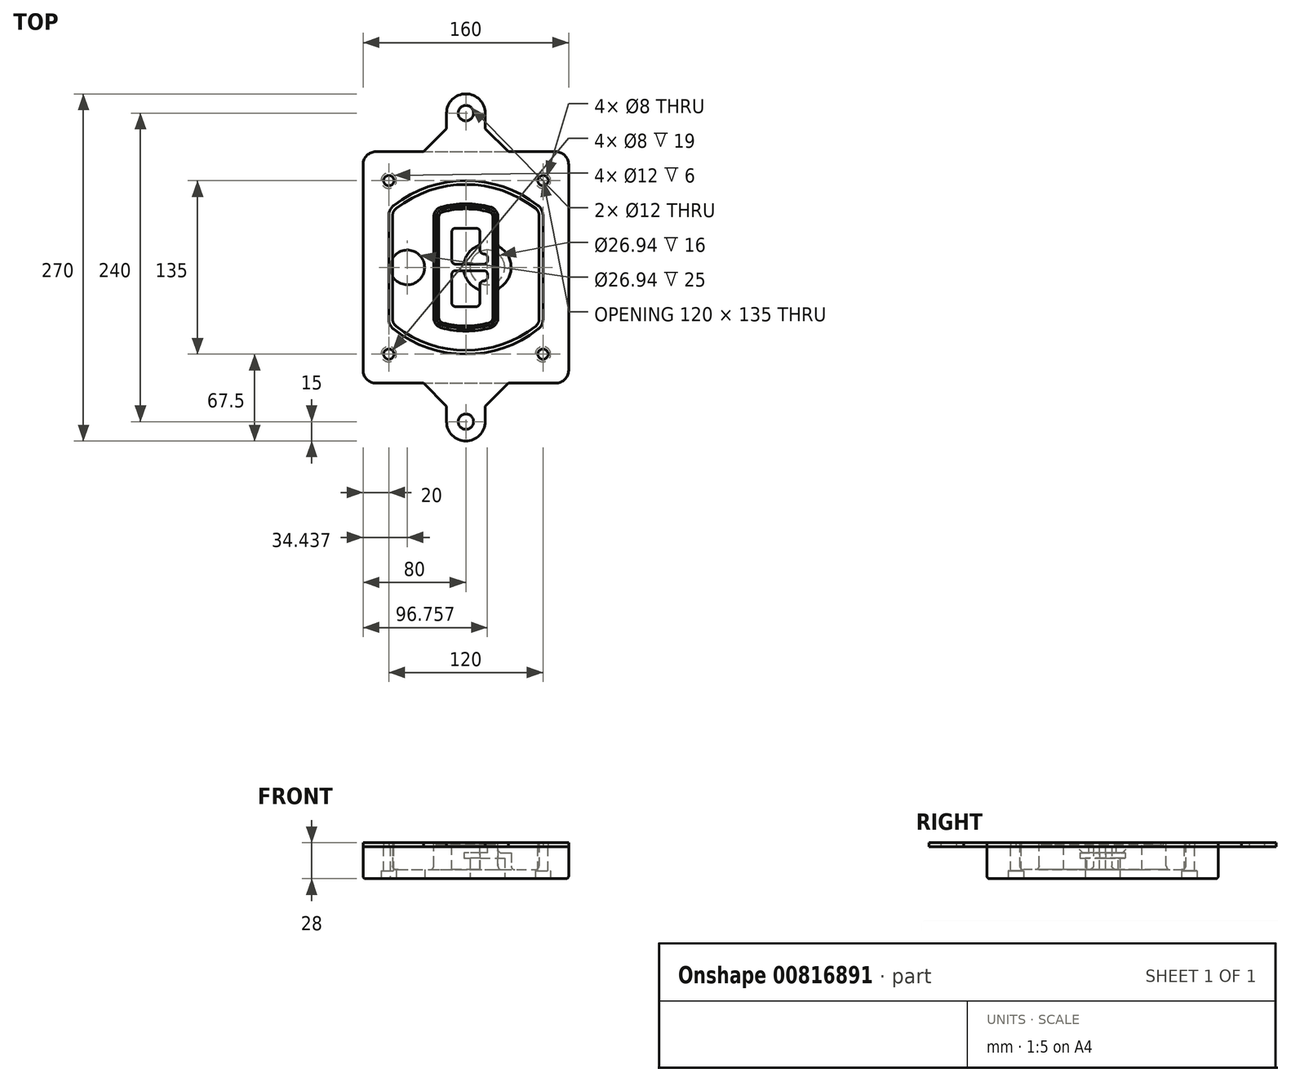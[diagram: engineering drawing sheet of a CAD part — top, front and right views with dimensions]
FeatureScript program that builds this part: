
annotation { "Feature Type Name" : "Feature", "Feature Type Description" : "" }
export const myFeature = defineFeature(function(context is Context, id is Id, definition is map)
    precondition{}
    {
        {
            var Q0;
            Q0=qCreatedBy(makeId("Top.planeOp"),FACE);
            var sketch = newSketch(context, id + "F0", { "sketchPlane" : qUnion([Q0])});
            skPoint(sketch, "E0.rect.middle", {"position": v(0, 0) * mm});
            skLineSegment(sketch, "E1.bottom", {"start": v(-70, -90) * mm, "end": v(70, -90) * mm});
            skLineSegment(sketch, "E1.top", {"start": v(-70, 90) * mm, "end": v(70, 90) * mm});
            skLineSegment(sketch, "E1.left", {"start": v(-80, -80) * mm, "end": v(-80, 80) * mm});
            skLineSegment(sketch, "E1.right", {"start": v(80, -80) * mm, "end": v(80, 80) * mm});
            skLineSegment(sketch, "E2", {"start": v(-80, 90) * mm, "end": v(80, -90) * mm, "construction": true});
            skLineSegment(sketch, "E3", {"start": v(80, 90) * mm, "end": v(-80, -90) * mm, "construction": true});
            skCircle(sketch, "E4", {"center": v(-60, 67.5) * mm, "radius": 4 * mm});
            skCircle(sketch, "E5", {"center": v(60, 67.5) * mm, "radius": 4 * mm});
            skCircle(sketch, "E6", {"center": v(60, -67.5) * mm, "radius": 4 * mm});
            skCircle(sketch, "E7", {"center": v(-60, -67.5) * mm, "radius": 4 * mm});
            skLineSegment(sketch, "E8", {"start": v(-60, 67.5) * mm, "end": v(60, 67.5) * mm, "construction": true});
            skLineSegment(sketch, "E9", {"start": v(60, 67.5) * mm, "end": v(60, -67.5) * mm, "construction": true});
            skLineSegment(sketch, "E10", {"start": v(60, -67.5) * mm, "end": v(-60, -67.5) * mm, "construction": true});
            skLineSegment(sketch, "E11", {"start": v(-60, -67.5) * mm, "end": v(-60, 67.5) * mm, "construction": true});
            skLineSegment(sketch, "E12", {"start": v(-60, 40.3) * mm, "end": v(-60, -40.3) * mm});
            skLineSegment(sketch, "E13", {"start": v(60, 40.3) * mm, "end": v(60, -40.3) * mm});
            skArc(sketch, "E14", {"start": v(56.15, 48.18) * mm, "mid": v(0, 67.5) * mm, "end": v(-56.15, 48.18) * mm});
            skArc(sketch, "E15", {"start": v(-56.15, -48.18) * mm, "mid": v(0, -67.5) * mm, "end": v(56.15, -48.18) * mm});
            skLineSegment(sketch, "E16", {"start": v(-60, 0) * mm, "end": v(60, 0) * mm, "construction": true});
            skPoint(sketch, "E17.visualSharp", {"position": v(-60, -45) * mm});
            skArc(sketch, "E17.filletArc", {"start": v(-60, -40.3) * mm, "mid": v(-58.99, -44.68) * mm, "end": v(-56.15, -48.18) * mm});
            skPoint(sketch, "E18.visualSharp", {"position": v(-60, 45) * mm});
            skArc(sketch, "E18.filletArc", {"start": v(-56.15, 48.18) * mm, "mid": v(-58.99, 44.68) * mm, "end": v(-60, 40.3) * mm});
            skPoint(sketch, "E19.visualSharp", {"position": v(60, 45) * mm});
            skArc(sketch, "E19.filletArc", {"start": v(60, 40.3) * mm, "mid": v(58.99, 44.68) * mm, "end": v(56.15, 48.18) * mm});
            skPoint(sketch, "E20.visualSharp", {"position": v(60, -45) * mm});
            skArc(sketch, "E20.filletArc", {"start": v(56.15, -48.18) * mm, "mid": v(58.99, -44.68) * mm, "end": v(60, -40.3) * mm});
            skPoint(sketch, "E21.visualSharp", {"position": v(-80, 90) * mm});
            skArc(sketch, "E21.filletArc", {"start": v(-70, 90) * mm, "mid": v(-77.07, 87.07) * mm, "end": v(-80, 80) * mm});
            skPoint(sketch, "E22.visualSharp", {"position": v(80, 90) * mm});
            skArc(sketch, "E22.filletArc", {"start": v(80, 80) * mm, "mid": v(77.07, 87.07) * mm, "end": v(70, 90) * mm});
            skPoint(sketch, "E23.visualSharp", {"position": v(80, -90) * mm});
            skArc(sketch, "E23.filletArc", {"start": v(70, -90) * mm, "mid": v(77.07, -87.07) * mm, "end": v(80, -80) * mm});
            skPoint(sketch, "E24.visualSharp", {"position": v(-80, -90) * mm});
            skArc(sketch, "E24.filletArc", {"start": v(-80, -80) * mm, "mid": v(-77.07, -87.07) * mm, "end": v(-70, -90) * mm});
            skArc(sketch, "E25.0", {"start": v(57, 40.3) * mm, "mid": v(56.3, 43.36) * mm, "end": v(54.3, 45.81) * mm});
            skLineSegment(sketch, "E25.1", {"start": v(57, 40.3) * mm, "end": v(57, -40.3) * mm});
            skArc(sketch, "E25.2", {"start": v(54.3, -45.81) * mm, "mid": v(56.3, -43.36) * mm, "end": v(57, -40.3) * mm});
            skArc(sketch, "E25.3", {"start": v(-54.3, -45.81) * mm, "mid": v(0, -64.5) * mm, "end": v(54.3, -45.81) * mm});
            skArc(sketch, "E25.4", {"start": v(-57, -40.3) * mm, "mid": v(-56.3, -43.36) * mm, "end": v(-54.3, -45.81) * mm});
            skArc(sketch, "E25.5", {"start": v(54.3, 45.81) * mm, "mid": v(0, 64.5) * mm, "end": v(-54.3, 45.81) * mm});
            skLineSegment(sketch, "E25.6", {"start": v(-57, 40.3) * mm, "end": v(-57, -40.3) * mm});
            skArc(sketch, "E25.7", {"start": v(-54.3, 45.81) * mm, "mid": v(-56.3, 43.36) * mm, "end": v(-57, 40.3) * mm});
            skArc(sketch, "E26.0", {"start": v(-58.62, 51.33) * mm, "mid": v(-62.58, 46.43) * mm, "end": v(-64, 40.3) * mm});
            skArc(sketch, "E26.1", {"start": v(58.62, 51.33) * mm, "mid": v(0, 71.5) * mm, "end": v(-58.62, 51.33) * mm});
            skArc(sketch, "E26.2", {"start": v(64, 40.3) * mm, "mid": v(62.58, 46.43) * mm, "end": v(58.62, 51.33) * mm});
            skLineSegment(sketch, "E26.3", {"start": v(64, 40.3) * mm, "end": v(64, -40.3) * mm});
            skArc(sketch, "E26.4", {"start": v(58.62, -51.33) * mm, "mid": v(62.58, -46.43) * mm, "end": v(64, -40.3) * mm});
            skLineSegment(sketch, "E26.5", {"start": v(-64, 40.3) * mm, "end": v(-64, -40.3) * mm});
            skArc(sketch, "E26.6", {"start": v(-58.62, -51.33) * mm, "mid": v(0, -71.5) * mm, "end": v(58.62, -51.33) * mm});
            skArc(sketch, "E26.7", {"start": v(-64, -40.3) * mm, "mid": v(-62.58, -46.43) * mm, "end": v(-58.62, -51.33) * mm});
            skSolve(sketch);
        }
        {
            var Q0;
            Q0=makeQuery(id+"F0.imprint","IMPRINT",FACE,{"disambiguationData":[TD([[makeQuery(id+"F0.imprint","IMPRINT",EDGE,{"derivedFrom":sQuery(id+"F0.wireOp",EDGE,"E1.bottom")}),1.0]])]});
            var Q1;
            Q1=makeQuery(id+"F0.imprint","IMPRINT",FACE,{"disambiguationData":[TD([[makeQuery(id+"F0.imprint","IMPRINT",EDGE,{"derivedFrom":sQuery(id+"F0.wireOp",EDGE,"E12")}),1.0]])]});
            var Q2;
            Q2=makeQuery(id+"F0.imprint","IMPRINT",FACE,{"disambiguationData":[TD([[makeQuery(id+"F0.imprint","IMPRINT",EDGE,{"derivedFrom":sQuery(id+"F0.wireOp",EDGE,"E25.0")}),1.0]])]});
            var Q3;
            Q3=makeQuery(id+"F0.imprint","IMPRINT",FACE,{"disambiguationData":[TD([[makeQuery(id+"F0.imprint","IMPRINT",EDGE,{"derivedFrom":sQuery(id+"F0.wireOp",EDGE,"E12")}),-1.0]])]});
            extrude(context, id + "F1", {"entities" : qUnion([Q0, Q1, Q2, Q3]), "oppositeDirection" : true, "depth" : 25 * mm});
        }
        {
            var Q0;
            Q0=makeQuery(id+"F0.imprint","IMPRINT",FACE,{"disambiguationData":[TD([[makeQuery(id+"F0.imprint","IMPRINT",EDGE,{"derivedFrom":sQuery(id+"F0.wireOp",EDGE,"E12")}),1.0]])]});
            extrude(context, id + "F2", {"entities" : qUnion([Q0]), "operationType" : NewBodyOperationType.ADD, "depth" : 3 * mm});
        }
        {
            var Q0;
            Q0=makeQuery(id+"F0.imprint","IMPRINT",FACE,{"disambiguationData":[TD([[makeQuery(id+"F0.imprint","IMPRINT",EDGE,{"derivedFrom":sQuery(id+"F0.wireOp",EDGE,"E25.0")}),1.0]])]});
            extrude(context, id + "F3", {"entities" : qUnion([Q0]), "operationType" : NewBodyOperationType.REMOVE, "oppositeDirection" : true, "depth" : 18 * mm});
        }
        {
            var Q0;
            Q0=makeQuery(id+"F2.opExtrude","CAP_FACE",FACE,{"disambiguationData":[OSD([sQuery(id+"F0.wireOp",EDGE,"E12"),sQuery(id+"F0.wireOp",EDGE,"E13"),sQuery(id+"F0.wireOp",EDGE,"E14"),sQuery(id+"F0.wireOp",EDGE,"E15"),sQuery(id+"F0.wireOp",EDGE,"E17.filletArc"),sQuery(id+"F0.wireOp",EDGE,"E18.filletArc"),sQuery(id+"F0.wireOp",EDGE,"E19.filletArc"),sQuery(id+"F0.wireOp",EDGE,"E20.filletArc"),sQuery(id+"F0.wireOp",EDGE,"E25.0"),sQuery(id+"F0.wireOp",EDGE,"E25.1"),sQuery(id+"F0.wireOp",EDGE,"E25.2"),sQuery(id+"F0.wireOp",EDGE,"E25.3"),sQuery(id+"F0.wireOp",EDGE,"E25.4"),sQuery(id+"F0.wireOp",EDGE,"E25.5"),sQuery(id+"F0.wireOp",EDGE,"E25.6"),sQuery(id+"F0.wireOp",EDGE,"E25.7")])],"isStart":false});
            var sketch = newSketch(context, id + "F4", { "sketchPlane" : qUnion([Q0])});
            skArc(sketch, "E27.0", {"start": v(-19.08, -46.97) * mm, "mid": v(0, -49.5) * mm, "end": v(19.08, -46.97) * mm});
            skArc(sketch, "E28.0", {"start": v(19.08, 46.97) * mm, "mid": v(0, 49.5) * mm, "end": v(-19.08, 46.97) * mm});
            skLineSegment(sketch, "E29", {"start": v(-25, 39.25) * mm, "end": v(-25, -39.25) * mm});
            skLineSegment(sketch, "E30", {"start": v(25, 39.25) * mm, "end": v(25, -39.25) * mm});
            skLineSegment(sketch, "E31", {"start": v(-25, 45.1) * mm, "end": v(25, 45.1) * mm, "construction": true});
            skLineSegment(sketch, "E32", {"start": v(-25, -45.1) * mm, "end": v(25, -45.1) * mm, "construction": true});
            skPoint(sketch, "E33.visualSharp", {"position": v(-25, 45.1) * mm});
            skArc(sketch, "E33.filletArc", {"start": v(-19.08, 46.97) * mm, "mid": v(-23.35, 44.11) * mm, "end": v(-25, 39.25) * mm});
            skPoint(sketch, "E34.visualSharp", {"position": v(25, 45.1) * mm});
            skArc(sketch, "E34.filletArc", {"start": v(25, 39.25) * mm, "mid": v(23.35, 44.11) * mm, "end": v(19.08, 46.97) * mm});
            skPoint(sketch, "E35.visualSharp", {"position": v(25, -45.1) * mm});
            skArc(sketch, "E35.filletArc", {"start": v(19.08, -46.97) * mm, "mid": v(23.35, -44.11) * mm, "end": v(25, -39.25) * mm});
            skPoint(sketch, "E36.visualSharp", {"position": v(-25, -45.1) * mm});
            skArc(sketch, "E36.filletArc", {"start": v(-25, -39.25) * mm, "mid": v(-23.35, -44.11) * mm, "end": v(-19.08, -46.97) * mm});
            skArc(sketch, "E37.0", {"start": v(54.3, 45.81) * mm, "mid": v(0, 64.5) * mm, "end": v(-54.3, 45.81) * mm});
            skArc(sketch, "E37.1", {"start": v(-54.3, 45.81) * mm, "mid": v(-56.3, 43.36) * mm, "end": v(-57, 40.3) * mm});
            skLineSegment(sketch, "E37.2", {"start": v(-57, 40.3) * mm, "end": v(-57, -40.3) * mm});
            skArc(sketch, "E37.3", {"start": v(-57, -40.3) * mm, "mid": v(-56.3, -43.36) * mm, "end": v(-54.3, -45.81) * mm});
            skArc(sketch, "E37.4", {"start": v(-54.3, -45.81) * mm, "mid": v(0, -64.5) * mm, "end": v(54.3, -45.81) * mm});
            skArc(sketch, "E37.5", {"start": v(54.3, -45.81) * mm, "mid": v(56.3, -43.36) * mm, "end": v(57, -40.3) * mm});
            skLineSegment(sketch, "E37.6", {"start": v(57, 40.3) * mm, "end": v(57, -40.3) * mm});
            skArc(sketch, "E37.7", {"start": v(57, 40.3) * mm, "mid": v(56.3, 43.36) * mm, "end": v(54.3, 45.81) * mm});
            skLineSegment(sketch, "E38.0", {"start": v(23, 39.25) * mm, "end": v(23, -39.25) * mm});
            skArc(sketch, "E38.1", {"start": v(18.56, -45.04) * mm, "mid": v(21.76, -42.9) * mm, "end": v(23, -39.25) * mm});
            skArc(sketch, "E38.2", {"start": v(-18.56, -45.04) * mm, "mid": v(0, -47.5) * mm, "end": v(18.56, -45.04) * mm});
            skArc(sketch, "E38.3", {"start": v(-23, -39.25) * mm, "mid": v(-21.76, -42.9) * mm, "end": v(-18.56, -45.04) * mm});
            skLineSegment(sketch, "E38.4", {"start": v(-23, 39.25) * mm, "end": v(-23, -39.25) * mm});
            skArc(sketch, "E38.5", {"start": v(23, 39.25) * mm, "mid": v(21.76, 42.9) * mm, "end": v(18.56, 45.04) * mm});
            skArc(sketch, "E38.6", {"start": v(-18.56, 45.04) * mm, "mid": v(-21.76, 42.9) * mm, "end": v(-23, 39.25) * mm});
            skArc(sketch, "E38.7", {"start": v(18.56, 45.04) * mm, "mid": v(0, 47.5) * mm, "end": v(-18.56, 45.04) * mm});
            skArc(sketch, "E39.0", {"start": v(21, 39.25) * mm, "mid": v(20.18, 41.68) * mm, "end": v(18.04, 43.1) * mm});
            skLineSegment(sketch, "E39.1", {"start": v(21, 39.25) * mm, "end": v(21, -39.25) * mm});
            skArc(sketch, "E39.2", {"start": v(18.04, -43.1) * mm, "mid": v(20.18, -41.68) * mm, "end": v(21, -39.25) * mm});
            skArc(sketch, "E39.3", {"start": v(-18.04, -43.1) * mm, "mid": v(0, -45.5) * mm, "end": v(18.04, -43.1) * mm});
            skArc(sketch, "E39.4", {"start": v(-21, -39.25) * mm, "mid": v(-20.18, -41.68) * mm, "end": v(-18.04, -43.1) * mm});
            skArc(sketch, "E39.5", {"start": v(18.04, 43.1) * mm, "mid": v(0, 45.5) * mm, "end": v(-18.04, 43.1) * mm});
            skLineSegment(sketch, "E39.6", {"start": v(-21, 39.25) * mm, "end": v(-21, -39.25) * mm});
            skArc(sketch, "E39.7", {"start": v(-18.04, 43.1) * mm, "mid": v(-20.18, 41.68) * mm, "end": v(-21, 39.25) * mm});
            skLineSegment(sketch, "E40", {"start": v(-25, 0) * mm, "end": v(25, 0) * mm, "construction": true});
            skLineSegment(sketch, "E41", {"start": v(-11, 5.5) * mm, "end": v(-11, 27.5) * mm});
            skLineSegment(sketch, "E42", {"start": v(-8, 30.5) * mm, "end": v(8, 30.5) * mm});
            skLineSegment(sketch, "E43", {"start": v(11, 27.5) * mm, "end": v(11, 13.5) * mm});
            skLineSegment(sketch, "E44", {"start": v(14, 10.5) * mm, "end": v(14, 10.5) * mm});
            skLineSegment(sketch, "E45", {"start": v(17, 7.5) * mm, "end": v(17, 5.5) * mm});
            skLineSegment(sketch, "E46", {"start": v(14, 2.5) * mm, "end": v(-8, 2.5) * mm});
            skPoint(sketch, "E47.visualSharp", {"position": v(-11, 30.5) * mm});
            skArc(sketch, "E47.filletArc", {"start": v(-8, 30.5) * mm, "mid": v(-10.12, 29.62) * mm, "end": v(-11, 27.5) * mm});
            skPoint(sketch, "E48.visualSharp", {"position": v(11, 30.5) * mm});
            skArc(sketch, "E48.filletArc", {"start": v(11, 27.5) * mm, "mid": v(10.12, 29.62) * mm, "end": v(8, 30.5) * mm});
            skPoint(sketch, "E49.visualSharp", {"position": v(11, 10.5) * mm});
            skArc(sketch, "E49.filletArc", {"start": v(11, 13.5) * mm, "mid": v(11.88, 11.38) * mm, "end": v(14, 10.5) * mm});
            skPoint(sketch, "E50.visualSharp", {"position": v(17, 10.5) * mm});
            skArc(sketch, "E50.filletArc", {"start": v(17, 7.5) * mm, "mid": v(16.12, 9.62) * mm, "end": v(14, 10.5) * mm});
            skPoint(sketch, "E51.visualSharp", {"position": v(17, 2.5) * mm});
            skArc(sketch, "E51.filletArc", {"start": v(14, 2.5) * mm, "mid": v(16.12, 3.38) * mm, "end": v(17, 5.5) * mm});
            skPoint(sketch, "E52.visualSharp", {"position": v(-11, 2.5) * mm});
            skArc(sketch, "E52.filletArc", {"start": v(-11, 5.5) * mm, "mid": v(-10.12, 3.38) * mm, "end": v(-8, 2.5) * mm});
            skLineSegment(sketch, "E53.0.MirrorCS", {"start": v(14, -2.5) * mm, "end": v(-8, -2.5) * mm});
            skArc(sketch, "E54.0.MirrorCS", {"start": v(-11, -5.5) * mm, "mid": v(-10.12, -3.38) * mm, "end": v(-8, -2.5) * mm});
            skLineSegment(sketch, "E55.0.MirrorCS", {"start": v(-11, -5.5) * mm, "end": v(-11, -27.5) * mm});
            skArc(sketch, "E56.0.MirrorCS", {"start": v(-8, -30.5) * mm, "mid": v(-10.12, -29.62) * mm, "end": v(-11, -27.5) * mm});
            skLineSegment(sketch, "E57.0.MirrorCS", {"start": v(-8, -30.5) * mm, "end": v(8, -30.5) * mm});
            skArc(sketch, "E58.0.MirrorCS", {"start": v(11, -27.5) * mm, "mid": v(10.12, -29.62) * mm, "end": v(8, -30.5) * mm});
            skLineSegment(sketch, "E59.0.MirrorCS", {"start": v(11, -27.5) * mm, "end": v(11, -13.5) * mm});
            skArc(sketch, "E60.0.MirrorCS", {"start": v(11, -13.5) * mm, "mid": v(11.88, -11.38) * mm, "end": v(14, -10.5) * mm});
            skArc(sketch, "E61.0.MirrorCS", {"start": v(17, -7.5) * mm, "mid": v(16.12, -9.62) * mm, "end": v(14, -10.5) * mm});
            skLineSegment(sketch, "E62.0.MirrorCS", {"start": v(17, -7.5) * mm, "end": v(17, -5.5) * mm});
            skArc(sketch, "E63.0.MirrorCS", {"start": v(14, -2.5) * mm, "mid": v(16.12, -3.38) * mm, "end": v(17, -5.5) * mm});
            skSolve(sketch);
        }
        {
            var Q0;
            Q0=makeQuery(id+"F4.imprint","IMPRINT",FACE,{"disambiguationData":[TD([[makeQuery(id+"F4.imprint","IMPRINT",EDGE,{"derivedFrom":sQuery(id+"F4.wireOp",EDGE,"E27.0")}),1.0]])]});
            var Q1;
            Q1=makeQuery(id+"F4.imprint","IMPRINT",FACE,{"disambiguationData":[TD([[makeQuery(id+"F4.imprint","IMPRINT",EDGE,{"derivedFrom":sQuery(id+"F4.wireOp",EDGE,"E38.0")}),-1.0]])]});
            var Q2;
            Q2=makeQuery(id+"F4.imprint","IMPRINT",FACE,{"disambiguationData":[TD([[makeQuery(id+"F4.imprint","IMPRINT",EDGE,{"derivedFrom":sQuery(id+"F4.wireOp",EDGE,"E39.0")}),1.0]])]});
            extrude(context, id + "F5", {"entities" : qUnion([Q0, Q1, Q2]), "operationType" : NewBodyOperationType.ADD, "endBound" : BoundingType.UP_TO_NEXT, "oppositeDirection" : true, "depth" : 25 * mm});
        }
        {
            var Q0;
            Q0=makeQuery(id+"F4.imprint","IMPRINT",FACE,{"disambiguationData":[TD([[makeQuery(id+"F4.imprint","IMPRINT",EDGE,{"derivedFrom":sQuery(id+"F4.wireOp",EDGE,"E38.0")}),-1.0]])]});
            extrude(context, id + "F6", {"entities" : qUnion([Q0]), "operationType" : NewBodyOperationType.REMOVE, "oppositeDirection" : true, "depth" : 2 * mm});
        }
        {
            var Q0;
            Q0=makeQuery(id+"F1.opExtrude","CAP_FACE",FACE,{"disambiguationData":[OSD([sQuery(id+"F0.wireOp",EDGE,"E1.bottom"),sQuery(id+"F0.wireOp",EDGE,"E1.top"),sQuery(id+"F0.wireOp",EDGE,"E1.left"),sQuery(id+"F0.wireOp",EDGE,"E1.right"),sQuery(id+"F0.wireOp",EDGE,"E4"),sQuery(id+"F0.wireOp",EDGE,"E5"),sQuery(id+"F0.wireOp",EDGE,"E6"),sQuery(id+"F0.wireOp",EDGE,"E7"),sQuery(id+"F0.wireOp",EDGE,"E21.filletArc"),sQuery(id+"F0.wireOp",EDGE,"E22.filletArc"),sQuery(id+"F0.wireOp",EDGE,"E23.filletArc"),sQuery(id+"F0.wireOp",EDGE,"E24.filletArc")])],"isStart":false});
            var sketch = newSketch(context, id + "F7", { "sketchPlane" : qUnion([Q0])});
            skCircle(sketch, "E64", {"center": v(16.76, 0) * mm, "radius": 13.47 * mm});
            skCircle(sketch, "E65", {"center": v(-45.56, 0) * mm, "radius": 13.47 * mm});
            skLineSegment(sketch, "E66", {"start": v(80, 0) * mm, "end": v(-80, 0) * mm});
            skCircle(sketch, "E67", {"center": v(16.76, 0) * mm, "radius": 18.47 * mm});
            skCircle(sketch, "E68", {"center": v(60, -67.5) * mm, "radius": 6 * mm});
            skCircle(sketch, "E69", {"center": v(-60, -67.5) * mm, "radius": 6 * mm});
            skCircle(sketch, "E70", {"center": v(-60, 67.5) * mm, "radius": 6 * mm});
            skCircle(sketch, "E71", {"center": v(60, 67.5) * mm, "radius": 6 * mm});
            skSolve(sketch);
        }
        {
            var Q0;
            {var subQ1=sQuery(id+"F7.wireOp",EDGE,"E66");var subQ4=sQuery(id+"F7.wireOp",EDGE,"E64");var subQ6=makeQuery(id+"F7.imprint","INTERSECT",VERTEX,{"disambiguationData":[OD(0.0)],"derivedFrom":[subQ4,subQ1]});Q0=makeQuery(id+"F7.imprint","IMPRINT",FACE,{"disambiguationData":[TD([[makeQuery(id+"F7.imprint","IMPRINT",EDGE,{"disambiguationData":[TD([[subQ6,-1.0]])],"derivedFrom":subQ4}),-1.0]])]});}
            var Q1;
            {var subQ0=sQuery(id+"F7.wireOp",EDGE,"E66");var subQ1=sQuery(id+"F7.wireOp",EDGE,"E64");var subQ3=makeQuery(id+"F7.imprint","INTERSECT",VERTEX,{"disambiguationData":[OD(0.0)],"derivedFrom":[subQ1,subQ0]});Q1=makeQuery(id+"F7.imprint","IMPRINT",FACE,{"disambiguationData":[TD([[makeQuery(id+"F7.imprint","IMPRINT",EDGE,{"disambiguationData":[TD([[subQ3,-1.0]])],"derivedFrom":subQ1}),1.0]])]});}
            var Q2;
            {var subQ0=sQuery(id+"F7.wireOp",EDGE,"E66");var subQ1=sQuery(id+"F7.wireOp",EDGE,"E64");var subQ3=makeQuery(id+"F7.imprint","INTERSECT",VERTEX,{"disambiguationData":[OD(0.0)],"derivedFrom":[subQ1,subQ0]});Q2=makeQuery(id+"F7.imprint","IMPRINT",FACE,{"disambiguationData":[TD([[makeQuery(id+"F7.imprint","IMPRINT",EDGE,{"disambiguationData":[TD([[subQ3,1.0]])],"derivedFrom":subQ1}),1.0]])]});}
            var Q3;
            {var subQ1=sQuery(id+"F7.wireOp",EDGE,"E66");var subQ4=sQuery(id+"F7.wireOp",EDGE,"E64");var subQ6=makeQuery(id+"F7.imprint","INTERSECT",VERTEX,{"disambiguationData":[OD(0.0)],"derivedFrom":[subQ4,subQ1]});Q3=makeQuery(id+"F7.imprint","IMPRINT",FACE,{"disambiguationData":[TD([[makeQuery(id+"F7.imprint","IMPRINT",EDGE,{"disambiguationData":[TD([[subQ6,1.0]])],"derivedFrom":subQ4}),-1.0]])]});}
            extrude(context, id + "F8", {"entities" : qUnion([Q0, Q1, Q2, Q3]), "operationType" : NewBodyOperationType.ADD, "oppositeDirection" : true, "depth" : 20 * mm});
        }
        {
            var Q0;
            {var subQ0=sQuery(id+"F7.wireOp",EDGE,"E66");var subQ1=sQuery(id+"F7.wireOp",EDGE,"E64");var subQ3=makeQuery(id+"F7.imprint","INTERSECT",VERTEX,{"disambiguationData":[OD(0.0)],"derivedFrom":[subQ1,subQ0]});Q0=makeQuery(id+"F7.imprint","IMPRINT",FACE,{"disambiguationData":[TD([[makeQuery(id+"F7.imprint","IMPRINT",EDGE,{"disambiguationData":[TD([[subQ3,-1.0]])],"derivedFrom":subQ1}),1.0]])]});}
            var Q1;
            {var subQ0=sQuery(id+"F7.wireOp",EDGE,"E66");var subQ1=sQuery(id+"F7.wireOp",EDGE,"E64");var subQ3=makeQuery(id+"F7.imprint","INTERSECT",VERTEX,{"disambiguationData":[OD(0.0)],"derivedFrom":[subQ1,subQ0]});Q1=makeQuery(id+"F7.imprint","IMPRINT",FACE,{"disambiguationData":[TD([[makeQuery(id+"F7.imprint","IMPRINT",EDGE,{"disambiguationData":[TD([[subQ3,1.0]])],"derivedFrom":subQ1}),1.0]])]});}
            extrude(context, id + "F9", {"entities" : qUnion([Q0, Q1]), "operationType" : NewBodyOperationType.REMOVE, "oppositeDirection" : true, "depth" : 16 * mm});
        }
        {
            var Q0;
            {var subQ0=sQuery(id+"F7.wireOp",EDGE,"E66");var subQ1=sQuery(id+"F7.wireOp",EDGE,"E65");var subQ3=makeQuery(id+"F7.imprint","INTERSECT",VERTEX,{"disambiguationData":[OD(0.0)],"derivedFrom":[subQ1,subQ0]});Q0=makeQuery(id+"F7.imprint","IMPRINT",FACE,{"disambiguationData":[TD([[makeQuery(id+"F7.imprint","IMPRINT",EDGE,{"disambiguationData":[TD([[subQ3,-1.0]])],"derivedFrom":subQ1}),1.0]])]});}
            var Q1;
            {var subQ0=sQuery(id+"F7.wireOp",EDGE,"E66");var subQ1=sQuery(id+"F7.wireOp",EDGE,"E65");var subQ3=makeQuery(id+"F7.imprint","INTERSECT",VERTEX,{"disambiguationData":[OD(0.0)],"derivedFrom":[subQ1,subQ0]});Q1=makeQuery(id+"F7.imprint","IMPRINT",FACE,{"disambiguationData":[TD([[makeQuery(id+"F7.imprint","IMPRINT",EDGE,{"disambiguationData":[TD([[subQ3,1.0]])],"derivedFrom":subQ1}),1.0]])]});}
            extrude(context, id + "F10", {"entities" : qUnion([Q0, Q1]), "operationType" : NewBodyOperationType.REMOVE, "oppositeDirection" : true, "depth" : 25 * mm});
        }
        {
            var Q0;
            Q0=makeQuery(id+"F7.imprint","IMPRINT",FACE,{"disambiguationData":[TD([[makeQuery(id+"F7.imprint","IMPRINT",EDGE,{"derivedFrom":sQuery(id+"F7.wireOp",EDGE,"E68")}),1.0]])]});
            var Q1;
            Q1=makeQuery(id+"F7.imprint","IMPRINT",FACE,{"disambiguationData":[TD([[makeQuery(id+"F7.imprint","IMPRINT",EDGE,{"derivedFrom":makeQuery(id+"F1.opExtrude","CAP_EDGE",EDGE,{"disambiguationData":[OSD([sQuery(id+"F0.wireOp",EDGE,"E5")])],"isStart":false})}),-1.0]])]});
            var Q2;
            Q2=makeQuery(id+"F7.imprint","IMPRINT",FACE,{"disambiguationData":[TD([[makeQuery(id+"F7.imprint","IMPRINT",EDGE,{"derivedFrom":sQuery(id+"F7.wireOp",EDGE,"E69")}),1.0]])]});
            var Q3;
            Q3=makeQuery(id+"F7.imprint","IMPRINT",FACE,{"disambiguationData":[TD([[makeQuery(id+"F7.imprint","IMPRINT",EDGE,{"derivedFrom":makeQuery(id+"F1.opExtrude","CAP_EDGE",EDGE,{"disambiguationData":[OSD([sQuery(id+"F0.wireOp",EDGE,"E4")])],"isStart":false})}),-1.0]])]});
            var Q4;
            Q4=makeQuery(id+"F7.imprint","IMPRINT",FACE,{"disambiguationData":[TD([[makeQuery(id+"F7.imprint","IMPRINT",EDGE,{"derivedFrom":sQuery(id+"F7.wireOp",EDGE,"E70")}),1.0]])]});
            var Q5;
            Q5=makeQuery(id+"F7.imprint","IMPRINT",FACE,{"disambiguationData":[TD([[makeQuery(id+"F7.imprint","IMPRINT",EDGE,{"derivedFrom":makeQuery(id+"F1.opExtrude","CAP_EDGE",EDGE,{"disambiguationData":[OSD([sQuery(id+"F0.wireOp",EDGE,"E7")])],"isStart":false})}),-1.0]])]});
            var Q6;
            Q6=makeQuery(id+"F7.imprint","IMPRINT",FACE,{"disambiguationData":[TD([[makeQuery(id+"F7.imprint","IMPRINT",EDGE,{"derivedFrom":sQuery(id+"F7.wireOp",EDGE,"E71")}),1.0]])]});
            var Q7;
            Q7=makeQuery(id+"F7.imprint","IMPRINT",FACE,{"disambiguationData":[TD([[makeQuery(id+"F7.imprint","IMPRINT",EDGE,{"derivedFrom":makeQuery(id+"F1.opExtrude","CAP_EDGE",EDGE,{"disambiguationData":[OSD([sQuery(id+"F0.wireOp",EDGE,"E6")])],"isStart":false})}),-1.0]])]});
            extrude(context, id + "F11", {"entities" : qUnion([Q0, Q1, Q2, Q3, Q4, Q5, Q6, Q7]), "operationType" : NewBodyOperationType.REMOVE, "oppositeDirection" : true, "depth" : 6 * mm});
        }
        {
            var Q0;
            Q0=makeQuery(id+"F9.boolean.opBoolean","COPY",FACE,{"derivedFrom":makeQuery(id+"F9.opExtrude","CAP_FACE",FACE,{"disambiguationData":[OSD([sQuery(id+"F7.wireOp",EDGE,"E64")])],"isStart":false})});
            var sketch = newSketch(context, id + "F12", { "sketchPlane" : qUnion([Q0])});
            skArc(sketch, "E72.0", {"start": v(11, 17.55) * mm, "mid": v(2.57, 11.82) * mm, "end": v(-1.54, 2.5) * mm});
            skArc(sketch, "E72.1", {"start": v(-1.54, -2.5) * mm, "mid": v(2.57, -11.82) * mm, "end": v(11, -17.55) * mm});
            skLineSegment(sketch, "E73", {"start": v(-1.54, -2.5) * mm, "end": v(14, -2.5) * mm});
            skLineSegment(sketch, "E74.0", {"start": v(14, 2.5) * mm, "end": v(-1.54, 2.5) * mm});
            skArc(sketch, "E74.1", {"start": v(14, 2.5) * mm, "mid": v(16.12, 3.38) * mm, "end": v(17, 5.5) * mm});
            skLineSegment(sketch, "E74.2", {"start": v(17, 7.5) * mm, "end": v(17, 5.5) * mm});
            skArc(sketch, "E74.3", {"start": v(17, 7.5) * mm, "mid": v(16.12, 9.62) * mm, "end": v(14, 10.5) * mm});
            skArc(sketch, "E74.4", {"start": v(11, 13.5) * mm, "mid": v(11.88, 11.38) * mm, "end": v(14, 10.5) * mm});
            skLineSegment(sketch, "E74.5", {"start": v(11, 17.55) * mm, "end": v(11, 13.5) * mm});
            skLineSegment(sketch, "E74.7", {"start": v(14, -2.5) * mm, "end": v(-1.54, -2.5) * mm});
            skArc(sketch, "E74.8", {"start": v(14, -2.5) * mm, "mid": v(16.12, -3.38) * mm, "end": v(17, -5.5) * mm});
            skLineSegment(sketch, "E74.9", {"start": v(17, -7.5) * mm, "end": v(17, -5.5) * mm});
            skArc(sketch, "E74.10", {"start": v(17, -7.5) * mm, "mid": v(16.12, -9.62) * mm, "end": v(14, -10.5) * mm});
            skArc(sketch, "E74.11", {"start": v(11, -13.5) * mm, "mid": v(11.88, -11.38) * mm, "end": v(14, -10.5) * mm});
            skLineSegment(sketch, "E74.12", {"start": v(11, -17.55) * mm, "end": v(11, -13.5) * mm});
            skPoint(sketch, "E75.orphan", {"position": v(11, -27.5) * mm});
            skPoint(sketch, "E76.orphan", {"position": v(-8, -2.5) * mm});
            skPoint(sketch, "E77.orphan", {"position": v(-8, 2.5) * mm});
            skPoint(sketch, "E78.orphan", {"position": v(11, 27.5) * mm});
            skSolve(sketch);
        }
        {
            var Q0;
            {var subQ7=sQuery(id+"F12.wireOp",EDGE,"E72.0");var subQ14=sQuery(id+"F12.wireOp",EDGE,"E72.1");var subQ16=sQuery(id+"F12.wireOp",EDGE,"E74.1");var subQ18=sQuery(id+"F12.wireOp",EDGE,"E74.8");Q0=qUnion([makeQuery(id+"F12.imprint","IMPRINT",FACE,{"disambiguationData":[TD([[makeQuery(id+"F12.imprint","IMPRINT",EDGE,{"derivedFrom":subQ7}),1.0]])]}),makeQuery(id+"F12.imprint","IMPRINT",FACE,{"disambiguationData":[TD([[makeQuery(id+"F12.imprint","IMPRINT",EDGE,{"derivedFrom":subQ14}),1.0]])]}),makeQuery(id+"F12.imprint","IMPRINT",FACE,{"disambiguationData":[TD([[makeQuery(id+"F12.imprint","IMPRINT",EDGE,{"derivedFrom":subQ16}),1.0]])]}),makeQuery(id+"F12.imprint","IMPRINT",FACE,{"disambiguationData":[TD([[makeQuery(id+"F12.imprint","IMPRINT",EDGE,{"derivedFrom":subQ18}),-1.0]])]})]);}
            var Q1;
            Q1=makeQuery(id+"F5.boolean.opBoolean","SPLIT",FACE,{"disambiguationData":[TD([makeQuery(id+"F5.opExtrude","SWEPT_FACE",FACE,{"disambiguationData":[OSD([sQuery(id+"F4.wireOp",EDGE,"E41")])]})])],"derivedFrom":makeQuery(id+"F3.boolean.opBoolean","COPY",FACE,{"derivedFrom":makeQuery(id+"F3.opExtrude","CAP_FACE",FACE,{"disambiguationData":[OSD([sQuery(id+"F0.wireOp",EDGE,"E25.0"),sQuery(id+"F0.wireOp",EDGE,"E25.1"),sQuery(id+"F0.wireOp",EDGE,"E25.2"),sQuery(id+"F0.wireOp",EDGE,"E25.3"),sQuery(id+"F0.wireOp",EDGE,"E25.4"),sQuery(id+"F0.wireOp",EDGE,"E25.5"),sQuery(id+"F0.wireOp",EDGE,"E25.6"),sQuery(id+"F0.wireOp",EDGE,"E25.7")])],"isStart":false})})});
            extrude(context, id + "F13", {"entities" : qUnion([Q0]), "operationType" : NewBodyOperationType.REMOVE, "endBound" : BoundingType.UP_TO_SURFACE, "endBoundEntityFace" : qUnion([Q1]), "depth" : 25 * mm});
        }
        {
            var Q0;
            Q0=makeQuery(id+"F3.boolean.opBoolean","COPY",EDGE,{"derivedFrom":makeQuery(id+"F3.opExtrude","CAP_EDGE",EDGE,{"disambiguationData":[OSD([sQuery(id+"F0.wireOp",EDGE,"E25.6")])],"isStart":false})});
            var Q1;
            Q1=makeQuery(id+"F8.boolean.opBoolean","INTERSECT",EDGE,{"derivedFrom":[makeQuery(id+"F5.opExtrude","SWEPT_FACE",FACE,{"disambiguationData":[OSD([sQuery(id+"F4.wireOp",EDGE,"E30")])]}),makeQuery(id+"F8.opExtrude","CAP_FACE",FACE,{"disambiguationData":[OSD([sQuery(id+"F7.wireOp",EDGE,"E67")])],"isStart":false})]});
            var Q2;
            Q2=makeQuery(id+"F8.boolean.opBoolean","INTERSECT",EDGE,{"disambiguationData":[OD(1.0)],"derivedFrom":[makeQuery(id+"F5.opExtrude","SWEPT_FACE",FACE,{"disambiguationData":[OSD([sQuery(id+"F4.wireOp",EDGE,"E30")])]}),makeQuery(id+"F8.opExtrude","SWEPT_FACE",FACE,{"disambiguationData":[OSD([sQuery(id+"F7.wireOp",EDGE,"E67")])]})]});
            var Q3;
            {var subQ0=sQuery(id+"F4.wireOp",EDGE,"E30");Q3=makeQuery(id+"F8.boolean.opBoolean","SPLIT",EDGE,{"disambiguationData":[TD([makeQuery(id+"F5.opExtrude","SWEPT_FACE",FACE,{"disambiguationData":[OSD([sQuery(id+"F4.wireOp",EDGE,"E35.filletArc")])]})])],"derivedFrom":makeQuery(id+"F5.opExtrude","CAP_EDGE",EDGE,{"disambiguationData":[OSD([subQ0])],"isStart":false})});}
            var Q4;
            {var subQ0=sQuery(id+"F0.wireOp",EDGE,"E25.7");var subQ1=sQuery(id+"F0.wireOp",EDGE,"E25.1");var subQ2=sQuery(id+"F0.wireOp",EDGE,"E25.6");var subQ3=sQuery(id+"F0.wireOp",EDGE,"E25.5");var subQ4=sQuery(id+"F0.wireOp",EDGE,"E25.4");var subQ5=sQuery(id+"F0.wireOp",EDGE,"E25.0");var subQ6=sQuery(id+"F0.wireOp",EDGE,"E25.2");var subQ7=sQuery(id+"F0.wireOp",EDGE,"E25.3");Q4=makeQuery(id+"F8.boolean.opBoolean","INTERSECT",EDGE,{"derivedFrom":[makeQuery(id+"F5.boolean.opBoolean","SPLIT",FACE,{"disambiguationData":[TD([makeQuery(id+"F2.opExtrude","SWEPT_FACE",FACE,{"disambiguationData":[OSD([subQ5])]})])],"derivedFrom":makeQuery(id+"F3.boolean.opBoolean","COPY",FACE,{"derivedFrom":makeQuery(id+"F3.opExtrude","CAP_FACE",FACE,{"disambiguationData":[OSD([subQ5,subQ1,subQ6,subQ7,subQ4,subQ3,subQ2,subQ0])],"isStart":false})})}),makeQuery(id+"F8.opExtrude","SWEPT_FACE",FACE,{"disambiguationData":[OSD([sQuery(id+"F7.wireOp",EDGE,"E67")])]})]});}
            var Q5;
            Q5=makeQuery(id+"F8.boolean.opBoolean","INTERSECT",EDGE,{"disambiguationData":[OD(0.0)],"derivedFrom":[makeQuery(id+"F5.opExtrude","SWEPT_FACE",FACE,{"disambiguationData":[OSD([sQuery(id+"F4.wireOp",EDGE,"E30")])]}),makeQuery(id+"F8.opExtrude","SWEPT_FACE",FACE,{"disambiguationData":[OSD([sQuery(id+"F7.wireOp",EDGE,"E67")])]})]});
            fillet(context, id + "F14", {"entities" : qUnion([Q0, Q1, Q2, Q3, Q4, Q5]), "radius" : 3 * mm, "tangentPropagation" : true, "allowEdgeOverflow" : false});
        }
        {
            var Q0;
            Q0=makeQuery(id+"F1.opExtrude","CAP_EDGE",EDGE,{"disambiguationData":[OSD([sQuery(id+"F0.wireOp",EDGE,"E1.bottom")])],"isStart":false});
            fillet(context, id + "F15", {"entities" : qUnion([Q0]), "radius" : 2 * mm, "tangentPropagation" : true, "allowEdgeOverflow" : false});
        }
        {
            var Q0;
            {var subQ0=sQuery(id+"F0.wireOp",EDGE,"E21.filletArc");var subQ1=sQuery(id+"F0.wireOp",EDGE,"E7");var subQ2=sQuery(id+"F0.wireOp",EDGE,"E6");var subQ3=sQuery(id+"F0.wireOp",EDGE,"E5");var subQ4=sQuery(id+"F0.wireOp",EDGE,"E4");var subQ5=sQuery(id+"F0.wireOp",EDGE,"E22.filletArc");var subQ6=sQuery(id+"F0.wireOp",EDGE,"E1.bottom");var subQ7=sQuery(id+"F0.wireOp",EDGE,"E1.right");var subQ8=sQuery(id+"F0.wireOp",EDGE,"E1.top");var subQ9=sQuery(id+"F0.wireOp",EDGE,"E1.left");var subQ10=sQuery(id+"F0.wireOp",EDGE,"E23.filletArc");var subQ11=sQuery(id+"F0.wireOp",EDGE,"E24.filletArc");Q0=makeQuery(id+"F2.boolean.opBoolean","SPLIT",FACE,{"disambiguationData":[TD([makeQuery(id+"F1.opExtrude","SWEPT_FACE",FACE,{"disambiguationData":[OSD([subQ6])]})])],"derivedFrom":makeQuery(id+"F1.opExtrude","CAP_FACE",FACE,{"disambiguationData":[OSD([subQ6,subQ8,subQ9,subQ7,subQ4,subQ3,subQ2,subQ1,subQ0,subQ5,subQ10,subQ11])],"isStart":true})});}
            var sketch = newSketch(context, id + "F16", { "sketchPlane" : qUnion([Q0])});
            skLineSegment(sketch, "E79", {"start": v(0, 90) * mm, "end": v(0, 120) * mm, "construction": true});
            skLineSegment(sketch, "E80", {"start": v(-15, 120) * mm, "end": v(-15, 108) * mm});
            skLineSegment(sketch, "E81", {"start": v(-15, 108) * mm, "end": v(-33, 90) * mm});
            skLineSegment(sketch, "E82", {"start": v(15, 108) * mm, "end": v(33, 90) * mm});
            skCircle(sketch, "E83", {"center": v(0, 120) * mm, "radius": 6 * mm});
            skArc(sketch, "E84", {"start": v(-15, 120) * mm, "mid": v(0, 135) * mm, "end": v(15, 120) * mm});
            skLineSegment(sketch, "E85", {"start": v(15, 120) * mm, "end": v(15, 108) * mm});
            skLineSegment(sketch, "E86", {"start": v(-80, 0) * mm, "end": v(80, 0) * mm, "construction": true});
            skLineSegment(sketch, "E87.MirrorCS", {"start": v(0, -90) * mm, "end": v(0, -120) * mm, "construction": true});
            skLineSegment(sketch, "E88.MirrorCS", {"start": v(-15, -120) * mm, "end": v(-15, -108) * mm});
            skLineSegment(sketch, "E89.MirrorCS", {"start": v(-15, -108) * mm, "end": v(-33, -90) * mm});
            skLineSegment(sketch, "E90.MirrorCS", {"start": v(15, -108) * mm, "end": v(33, -90) * mm});
            skCircle(sketch, "E91.MirrorC", {"center": v(0, -120) * mm, "radius": 6 * mm});
            skArc(sketch, "E92.MirrorCS", {"start": v(-15, -120) * mm, "mid": v(0, -135) * mm, "end": v(15, -120) * mm});
            skLineSegment(sketch, "E93.MirrorCS", {"start": v(15, -120) * mm, "end": v(15, -108) * mm});
            skSolve(sketch);
        }
        {
            var Q0;
            Q0=makeQuery(id+"F16.imprint","IMPRINT",FACE,{"disambiguationData":[TD([[makeQuery(id+"F16.imprint","IMPRINT",EDGE,{"derivedFrom":sQuery(id+"F16.wireOp",EDGE,"E80")}),1.0]])]});
            var Q1;
            Q1=makeQuery(id+"F16.imprint","IMPRINT",FACE,{"disambiguationData":[TD([[makeQuery(id+"F16.imprint","IMPRINT",EDGE,{"derivedFrom":makeQuery(id+"F1.opExtrude","CAP_EDGE",EDGE,{"disambiguationData":[OSD([sQuery(id+"F0.wireOp",EDGE,"E1.left")])],"isStart":true})}),-1.0]])]});
            var Q2;
            Q2=makeQuery(id+"F16.imprint","IMPRINT",FACE,{"disambiguationData":[TD([[makeQuery(id+"F16.imprint","IMPRINT",EDGE,{"derivedFrom":sQuery(id+"F16.wireOp",EDGE,"E88.MirrorCS")}),-1.0]])]});
            var Q3;
            Q3=makeQuery(id+"F2.opExtrude","CAP_FACE",FACE,{"disambiguationData":[OSD([sQuery(id+"F0.wireOp",EDGE,"E12"),sQuery(id+"F0.wireOp",EDGE,"E13"),sQuery(id+"F0.wireOp",EDGE,"E14"),sQuery(id+"F0.wireOp",EDGE,"E15"),sQuery(id+"F0.wireOp",EDGE,"E17.filletArc"),sQuery(id+"F0.wireOp",EDGE,"E18.filletArc"),sQuery(id+"F0.wireOp",EDGE,"E19.filletArc"),sQuery(id+"F0.wireOp",EDGE,"E20.filletArc"),sQuery(id+"F0.wireOp",EDGE,"E25.0"),sQuery(id+"F0.wireOp",EDGE,"E25.1"),sQuery(id+"F0.wireOp",EDGE,"E25.2"),sQuery(id+"F0.wireOp",EDGE,"E25.3"),sQuery(id+"F0.wireOp",EDGE,"E25.4"),sQuery(id+"F0.wireOp",EDGE,"E25.5"),sQuery(id+"F0.wireOp",EDGE,"E25.6"),sQuery(id+"F0.wireOp",EDGE,"E25.7")])],"isStart":false});
            extrude(context, id + "F17", {"entities" : qUnion([Q0, Q1, Q2]), "endBound" : BoundingType.UP_TO_SURFACE, "depth" : 25 * mm, "endBoundEntityFace" : qUnion([Q3]), "offsetDistance" : 25 * mm});
        }
    });
